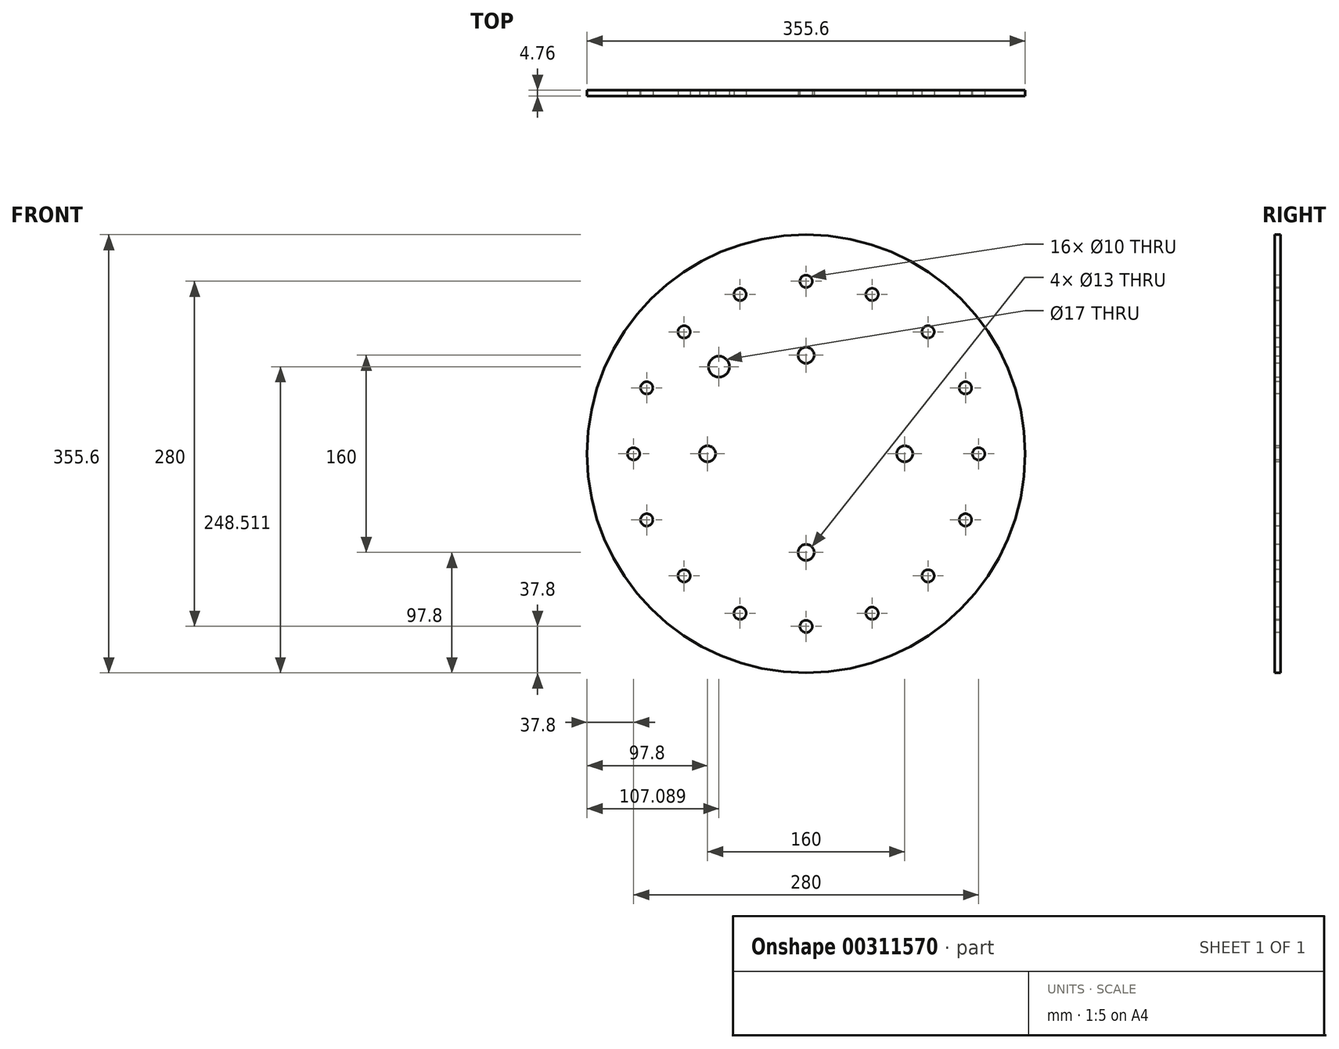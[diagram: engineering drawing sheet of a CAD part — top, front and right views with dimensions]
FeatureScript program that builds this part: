
annotation { "Feature Type Name" : "Feature", "Feature Type Description" : "" }
export const myFeature = defineFeature(function(context is Context, id is Id, definition is map)
    precondition{}
    {
        {
            var Q0;
            Q0=qCreatedBy(makeId("Front.planeOp"),FACE);
            var sketch = newSketch(context, id + "F0", { "sketchPlane" : qUnion([Q0])});
            skCircle(sketch, "E0", {"center": v(0, 0) * mm, "radius": 177.8 * mm});
            skSolve(sketch);
        }
        {
            var Q0;
            Q0 = qSketchRegion(id + "F0", true);
            var Q1;
            Q1=makeQuery(id+"F0.imprint","IMPRINT",FACE,{"disambiguationData":[TD([[makeQuery(id+"F0.imprint","IMPRINT",EDGE,{"derivedFrom":sQuery(id+"F0.wireOp",EDGE,"E0")}),1.0]])]});
            extrude(context, id + "F1", {"entities" : qUnion([Q0, Q1]), "depth" : 4.76 * mm});
        }
        {
            var Q0;
            Q0=makeQuery(id+"F1.opExtrude","CAP_FACE",FACE,{"disambiguationData":[OSD([sQuery(id+"F0.wireOp",EDGE,"E0")])],"isStart":false});
            var sketch = newSketch(context, id + "F2", { "sketchPlane" : qUnion([Q0])});
            skCircle(sketch, "E1", {"center": v(0, 0) * mm, "radius": 140 * mm});
            skPoint(sketch, "E2", {"position": v(0, 140) * mm});
            skPoint(sketch, "E3.1.0", {"position": v(53.58, 129.34) * mm});
            skPoint(sketch, "E3.2.0", {"position": v(99, 99) * mm});
            skPoint(sketch, "E3.3.0", {"position": v(129.34, 53.58) * mm});
            skPoint(sketch, "E3.4.0", {"position": v(140, 0) * mm});
            skLineSegment(sketch, "E3.anchor1", {"start": v(0, 0) * mm, "end": v(0, 140) * mm, "construction": true});
            skLineSegment(sketch, "E3.anchor2", {"start": v(0, 0) * mm, "end": v(140, 0) * mm, "construction": true});
            skPoint(sketch, "E4.1.0", {"position": v(129.34, -53.58) * mm});
            skPoint(sketch, "E4.2.0", {"position": v(99, -99) * mm});
            skPoint(sketch, "E4.3.0", {"position": v(53.58, -129.34) * mm});
            skPoint(sketch, "E4.4.0", {"position": v(0, -140) * mm});
            skLineSegment(sketch, "E4.anchor2", {"start": v(0, 0) * mm, "end": v(0, -140) * mm, "construction": true});
            skPoint(sketch, "E5.1.0", {"position": v(-53.58, -129.34) * mm});
            skPoint(sketch, "E5.2.0", {"position": v(-99, -99) * mm});
            skPoint(sketch, "E5.3.0", {"position": v(-129.34, -53.58) * mm});
            skPoint(sketch, "E5.4.0", {"position": v(-140, 0) * mm});
            skLineSegment(sketch, "E5.anchor2", {"start": v(0, 0) * mm, "end": v(-140, 0) * mm, "construction": true});
            skPoint(sketch, "E6.1.0", {"position": v(-129.34, 53.58) * mm});
            skPoint(sketch, "E6.2.0", {"position": v(-99, 99) * mm});
            skPoint(sketch, "E6.3.0", {"position": v(-53.58, 129.34) * mm});
            skSolve(sketch);
        }
        {
            var Q0;
            Q0=sQuery(id+"F2.wireOp",VERTEX,"E2");
            var Q1;
            Q1=sQuery(id+"F2.wireOp",VERTEX,"E3.1.0");
            var Q2;
            Q2=sQuery(id+"F2.wireOp",VERTEX,"E3.2.0");
            var Q3;
            Q3=sQuery(id+"F2.wireOp",VERTEX,"E3.3.0");
            var Q4;
            Q4=sQuery(id+"F2.wireOp",VERTEX,"E3.4.0");
            var Q5;
            Q5=sQuery(id+"F2.wireOp",VERTEX,"E4.1.0");
            var Q6;
            Q6=sQuery(id+"F2.wireOp",VERTEX,"E4.2.0");
            var Q7;
            Q7=sQuery(id+"F2.wireOp",VERTEX,"E4.3.0");
            var Q8;
            Q8=sQuery(id+"F2.wireOp",VERTEX,"E4.4.0");
            var Q9;
            Q9=sQuery(id+"F2.wireOp",VERTEX,"E5.1.0");
            var Q10;
            Q10=sQuery(id+"F2.wireOp",VERTEX,"E5.2.0");
            var Q11;
            Q11=sQuery(id+"F2.wireOp",VERTEX,"E5.3.0");
            var Q12;
            Q12=sQuery(id+"F2.wireOp",VERTEX,"E5.4.0");
            var Q13;
            Q13=sQuery(id+"F2.wireOp",VERTEX,"E6.1.0");
            var Q14;
            Q14=sQuery(id+"F2.wireOp",VERTEX,"E6.2.0");
            var Q15;
            Q15=sQuery(id+"F2.wireOp",VERTEX,"E6.3.0");
            var Q16;
            Q16=sQuery(id+"F2.wireOp",VERTEX,"E6.3.0");
            var Q17;
            Q17=makeQuery(id+"F1.opExtrude","SWEPT_BODY",BODY,{"disambiguationData":[OSD([sQuery(id+"F0.wireOp",EDGE,"E0")])]});
            hole(context, id + "F3", {"style" : HoleStyle.SIMPLE, "endStyle" : HoleEndStyle.THROUGH, "holeDiameter" : 10 * mm, "tappedDepth" : 12 * mm, "tapClearance" : 3, "locations" : qUnion([Q0, Q1, Q2, Q3, Q4, Q5, Q6, Q7, Q8, Q9, Q10, Q11, Q12, Q13, Q14, Q15, Q16]), "scope" : qUnion([Q17])});
        }
        {
            var Q0;
            Q0=makeQuery(id+"F2.imprint","IMPRINT",FACE,{"disambiguationData":[TD([[makeQuery(id+"F2.imprint","IMPRINT",EDGE,{"derivedFrom":sQuery(id+"F2.wireOp",EDGE,"E1")}),1.0]])]});
            var sketch = newSketch(context, id + "F4", { "sketchPlane" : qUnion([Q0])});
            skPoint(sketch, "E7", {"position": v(0, 80) * mm});
            skPoint(sketch, "E8", {"position": v(0, -80) * mm});
            skPoint(sketch, "E9", {"position": v(80, 0) * mm});
            skPoint(sketch, "E10", {"position": v(-80, 0) * mm});
            skPoint(sketch, "E11", {"position": v(0, 0) * mm});
            skSolve(sketch);
        }
        {
            var Q0;
            Q0=sQuery(id+"F4.wireOp",VERTEX,"E7");
            var Q1;
            Q1=sQuery(id+"F4.wireOp",VERTEX,"E9");
            var Q2;
            Q2=sQuery(id+"F4.wireOp",VERTEX,"E8");
            var Q3;
            Q3=sQuery(id+"F4.wireOp",VERTEX,"E10");
            var Q4;
            Q4=makeQuery(id+"F1.opExtrude","SWEPT_BODY",BODY,{"disambiguationData":[OSD([sQuery(id+"F0.wireOp",EDGE,"E0")])]});
            hole(context, id + "F5", {"style" : HoleStyle.SIMPLE, "endStyle" : HoleEndStyle.THROUGH, "holeDiameter" : 13 * mm, "tappedDepth" : 12 * mm, "tapClearance" : 3, "locations" : qUnion([Q0, Q1, Q2, Q3]), "scope" : qUnion([Q4])});
        }
        {
            var Q0;
            Q0=makeQuery(id+"F2.imprint","IMPRINT",FACE,{"disambiguationData":[TD([[makeQuery(id+"F2.imprint","IMPRINT",EDGE,{"derivedFrom":sQuery(id+"F2.wireOp",EDGE,"E1")}),1.0]])]});
            var sketch = newSketch(context, id + "F6", { "sketchPlane" : qUnion([Q0])});
            skPoint(sketch, "E12", {"position": v(-70.71, 70.71) * mm});
            skPoint(sketch, "E13", {"position": v(0, 0) * mm});
            skSolve(sketch);
        }
        {
            var Q0;
            Q0=sQuery(id+"F6.wireOp",VERTEX,"E12");
            var Q1;
            Q1=makeQuery(id+"F1.opExtrude","SWEPT_BODY",BODY,{"disambiguationData":[OSD([sQuery(id+"F0.wireOp",EDGE,"E0")])]});
            hole(context, id + "F7", {"style" : HoleStyle.SIMPLE, "endStyle" : HoleEndStyle.THROUGH, "holeDiameter" : 17 * mm, "tappedDepth" : 12 * mm, "tapClearance" : 3, "locations" : qUnion([Q0]), "scope" : qUnion([Q1])});
        }
    });
